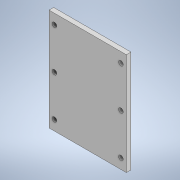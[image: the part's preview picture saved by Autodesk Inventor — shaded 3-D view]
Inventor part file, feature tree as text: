
AUTODESK INVENTOR PART (.ipt)
format: ipt  version: 2022 (Build 260153000, 153)  size: 123,904 bytes
history: native  units: in
note: dims shown in document units (in); Inventor stores cm internally (conversion verified against a paired STEP export)
features: extrude x2, sketch x2, projected_geometry x1
ambient origin geometry x8: Origin, YZ Plane, XZ Plane, XY Plane, X Axis, Y Axis, Z Axis, Center Point
bodies: Solid1 (feature_tree)
feature tree (5):
  extrude  "Extrusion1"  Depth=2.5984in
  extrude  "Extrusion2"  Depth=0.1181in
  sketch  "Sketch1"  dims[d0=2.5984in d1=1.4173in]
  sketch  "Sketch2"  dims[d2=0.1181in d3=0.0in d4=0.2756in d5=0.2559in d6=0.2559in d7=0.1181in d8=0.1181in d9=0.1181in d10=0.1181in d11=0.0in]
  projected_geometry  "Projected Loop1"
